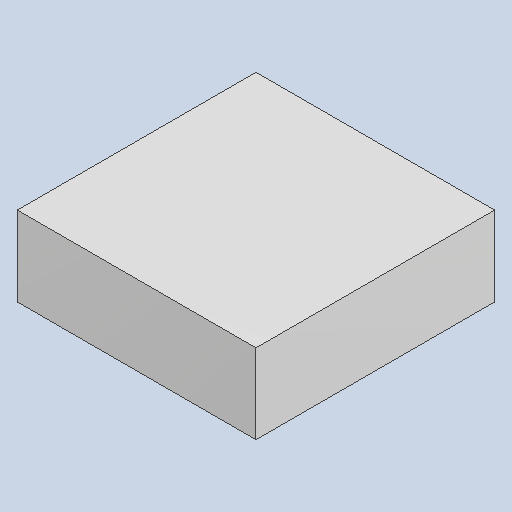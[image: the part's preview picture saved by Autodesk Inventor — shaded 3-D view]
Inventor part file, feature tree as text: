
AUTODESK INVENTOR PART (.ipt)
format: ipt  version: 2023.4 (Build 274418000, 418)  size: 79,872 bytes
history: native  units: mm
features: extrude x1
ambient origin geometry x8: Origin, YZ Plane, XZ Plane, XY Plane, X Axis, Y Axis, Z Axis, Center Point
bodies: Solid1 (feature_tree)
feature tree (1):
  extrude  "Extruded_61"  [1 undecoded]
note: 1 required parameter value undecoded (feature->parameter linkage not recoverable at this tier; creation-order binding heuristic only, values carry confidence <= 0.55)
